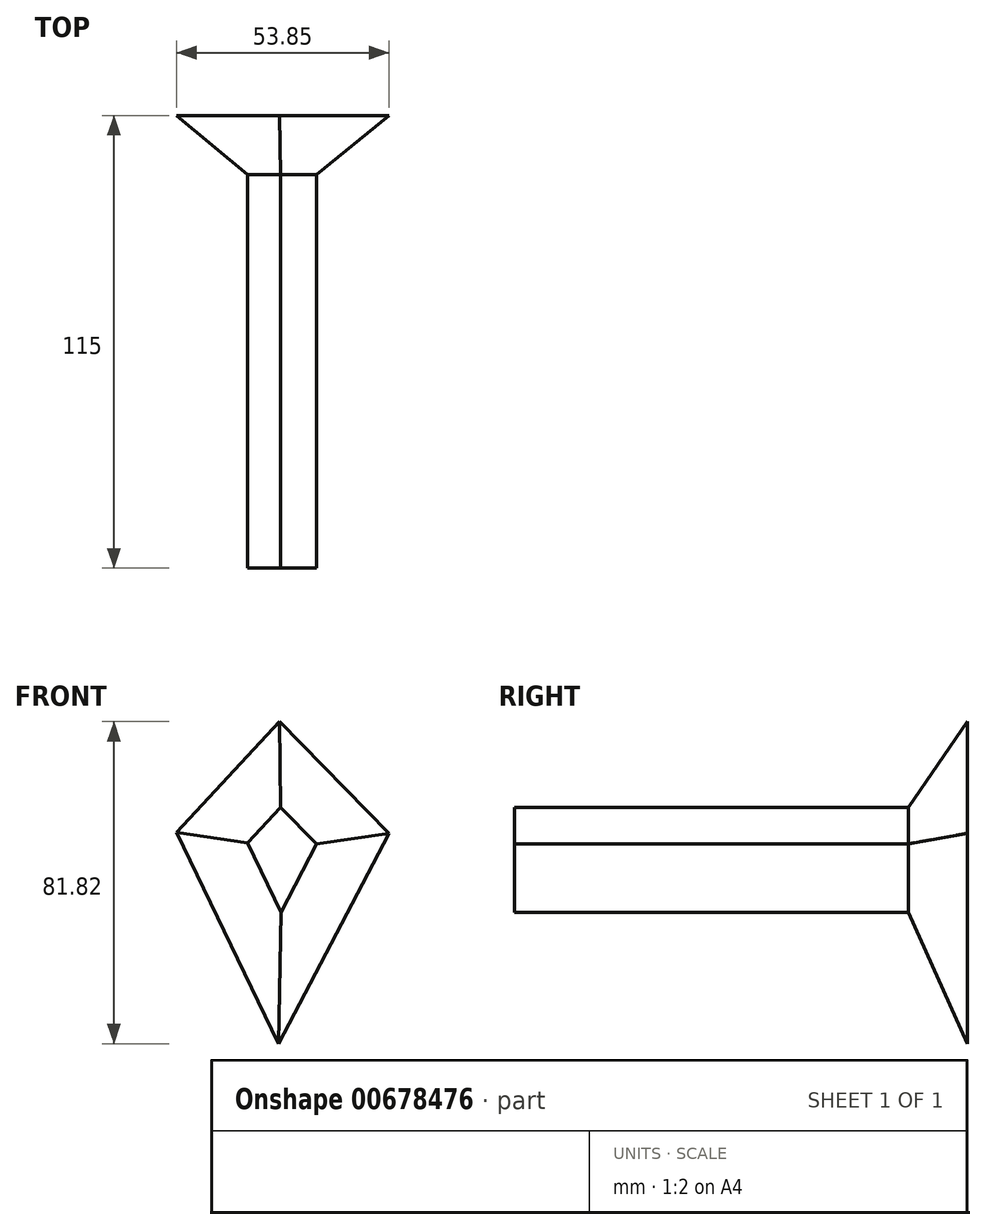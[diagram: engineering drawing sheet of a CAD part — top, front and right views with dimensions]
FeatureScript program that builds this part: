
annotation { "Feature Type Name" : "Feature", "Feature Type Description" : "" }
export const myFeature = defineFeature(function(context is Context, id is Id, definition is map)
    precondition{}
    {
        {
            var Q0;
            Q0=qCreatedBy(makeId("Front.planeOp"),FACE);
            var sketch = newSketch(context, id + "F0", { "sketchPlane" : qUnion([Q0])});
            skLineSegment(sketch, "E0", {"start": v(-8.62, 2.15) * mm, "end": v(-0.14, 11.31) * mm});
            skLineSegment(sketch, "E1", {"start": v(-0.23, 11.31) * mm, "end": v(8.94, 1.95) * mm});
            skLineSegment(sketch, "E2", {"start": v(8.94, 1.95) * mm, "end": v(-0.14, -15.41) * mm});
            skLineSegment(sketch, "E3", {"start": v(-0.14, -15.41) * mm, "end": v(-8.62, 2.15) * mm});
            skSolve(sketch);
        }
        {
            var Q0;
            {var subQ4=sQuery(id+"F0.wireOp",EDGE,"E2");Q0=makeQuery(id+"F0.imprint","IMPRINT",FACE,{"disambiguationData":[TD([[makeQuery(id+"F0.imprint","IMPRINT",EDGE,{"derivedFrom":subQ4}),-1.0]])]});}
            extrude(context, id + "F1", {"entities" : qUnion([Q0]), "depth" : 100 * mm, "offsetDistance" : 25 * mm});
        }
        {
            var Q0;
            Q0=makeQuery(id+"F1.opExtrude","CAP_FACE",FACE,{"disambiguationData":[OSD([sQuery(id+"F0.wireOp",EDGE,"E0"),sQuery(id+"F0.wireOp",EDGE,"E1"),sQuery(id+"F0.wireOp",EDGE,"E2"),sQuery(id+"F0.wireOp",EDGE,"E3")])],"isStart":true});
            extrude(context, id + "F2", {"entities" : qUnion([Q0]), "operationType" : NewBodyOperationType.ADD, "depth" : 15 * mm, "offsetDistance" : 25 * mm, "hasDraft" : true, "draftAngle" : 45 * degree});
        }
    });
